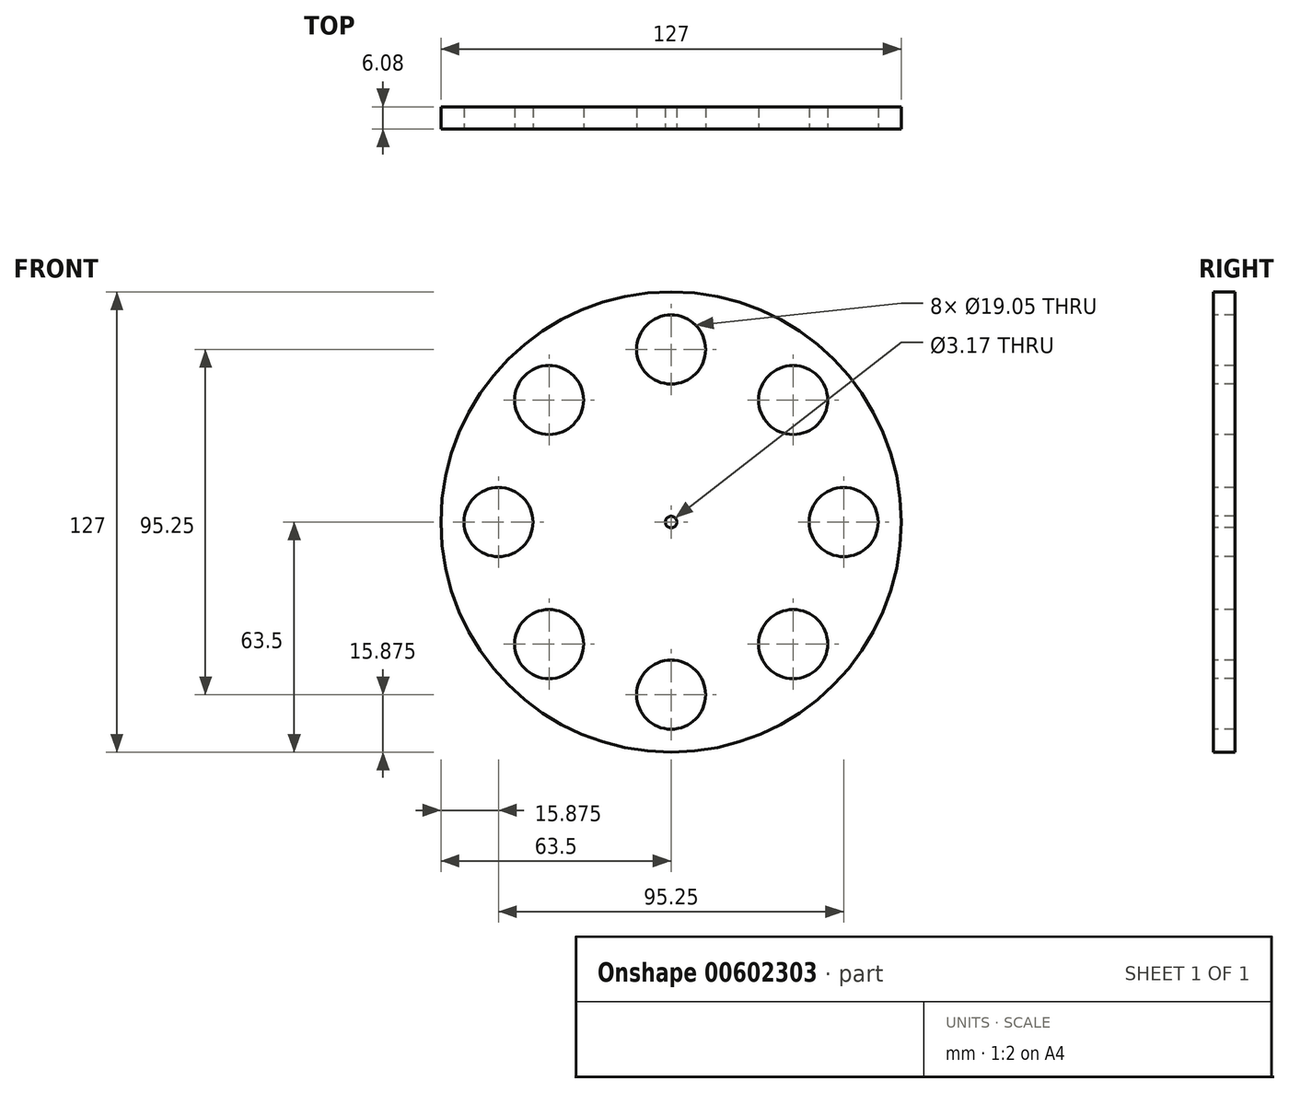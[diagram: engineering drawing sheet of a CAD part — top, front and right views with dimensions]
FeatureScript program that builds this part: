
annotation { "Feature Type Name" : "Feature", "Feature Type Description" : "" }
export const myFeature = defineFeature(function(context is Context, id is Id, definition is map)
    precondition{}
    {
        {
            var Q0;
            Q0=qCreatedBy(makeId("Front.planeOp"),FACE);
            var sketch = newSketch(context, id + "F0", { "sketchPlane" : qUnion([Q0])});
            skCircle(sketch, "E0", {"center": v(0, 0) * mm, "radius": 63.5 * mm});
            skSolve(sketch);
        }
        {
            var Q0;
            Q0=qSketchRegion(id+"F0",true);
            extrude(context, id + "F1", {"entities" : qUnion([Q0]), "depth" : 6.08 * mm});
        }
        {
            var Q0;
            Q0=makeQuery(id+"F1.opExtrude","CAP_FACE",FACE,{"disambiguationData":[OSD([sQuery(id+"F0.wireOp",EDGE,"E0")])],"isStart":false});
            var sketch = newSketch(context, id + "F2", { "sketchPlane" : qUnion([Q0])});
            skCircle(sketch, "E1", {"center": v(0, 0) * mm, "radius": 1.59 * mm});
            skLineSegment(sketch, "E2", {"start": v(-63.5, 0) * mm, "end": v(0, 0) * mm});
            skLineSegment(sketch, "E3", {"start": v(0, 63.5) * mm, "end": v(0, 0) * mm});
            skLineSegment(sketch, "E4", {"start": v(0, 0) * mm, "end": v(0, -63.5) * mm});
            skLineSegment(sketch, "E5", {"start": v(0, -63.5) * mm, "end": v(0, 0) * mm});
            skLineSegment(sketch, "E6", {"start": v(63.5, 0) * mm, "end": v(0, 0) * mm});
            skLineSegment(sketch, "E7", {"start": v(0, 0) * mm, "end": v(-44.9, 44.9) * mm});
            skLineSegment(sketch, "E8", {"start": v(0, 0) * mm, "end": v(44.9, 44.9) * mm});
            skLineSegment(sketch, "E9", {"start": v(0, 0) * mm, "end": v(44.9, -44.9) * mm});
            skLineSegment(sketch, "E10", {"start": v(0, 0) * mm, "end": v(-44.9, -44.9) * mm});
            skLineSegment(sketch, "E11", {"start": v(0, 0) * mm, "end": v(-58.67, -24.3) * mm});
            skLineSegment(sketch, "E12", {"start": v(0, 0) * mm, "end": v(-24.3, -58.67) * mm});
            skLineSegment(sketch, "E13", {"start": v(0, 0) * mm, "end": v(24.3, -58.67) * mm});
            skLineSegment(sketch, "E14", {"start": v(0, 0) * mm, "end": v(58.67, -24.3) * mm});
            skLineSegment(sketch, "E15", {"start": v(0, 0) * mm, "end": v(58.67, 24.3) * mm});
            skLineSegment(sketch, "E16", {"start": v(0, 0) * mm, "end": v(24.3, 58.67) * mm});
            skLineSegment(sketch, "E17", {"start": v(0, 0) * mm, "end": v(-24.3, 58.67) * mm});
            skLineSegment(sketch, "E18", {"start": v(0, 0) * mm, "end": v(-58.67, 24.3) * mm});
            skLineSegment(sketch, "E19", {"start": v(-22.45, 22.45) * mm, "end": v(-44.9, 44.9) * mm});
            skCircle(sketch, "E20", {"center": v(-33.68, 33.68) * mm, "radius": 9.53 * mm});
            skLineSegment(sketch, "E21", {"start": v(0, 31.75) * mm, "end": v(0, 63.5) * mm});
            skLineSegment(sketch, "E22", {"start": v(44.9, 44.9) * mm, "end": v(22.45, 22.45) * mm});
            skLineSegment(sketch, "E23", {"start": v(31.75, 0) * mm, "end": v(63.5, 0) * mm});
            skLineSegment(sketch, "E24", {"start": v(44.9, -44.9) * mm, "end": v(22.45, -22.45) * mm});
            skLineSegment(sketch, "E25", {"start": v(0, -63.5) * mm, "end": v(0, -31.75) * mm});
            skLineSegment(sketch, "E26", {"start": v(-44.9, -44.9) * mm, "end": v(-22.45, -22.45) * mm});
            skLineSegment(sketch, "E27", {"start": v(-63.5, 0) * mm, "end": v(-31.75, 0) * mm});
            skCircle(sketch, "E28", {"center": v(-47.62, 0) * mm, "radius": 9.53 * mm});
            skCircle(sketch, "E29", {"center": v(0, 47.62) * mm, "radius": 9.53 * mm});
            skCircle(sketch, "E30", {"center": v(33.68, 33.68) * mm, "radius": 9.53 * mm});
            skCircle(sketch, "E31", {"center": v(47.62, 0) * mm, "radius": 9.53 * mm});
            skCircle(sketch, "E32", {"center": v(33.68, -33.68) * mm, "radius": 9.53 * mm});
            skCircle(sketch, "E33", {"center": v(0, -47.62) * mm, "radius": 9.53 * mm});
            skCircle(sketch, "E34", {"center": v(-33.68, -33.68) * mm, "radius": 9.53 * mm});
            skSolve(sketch);
        }
        {
            var Q0;
            Q0=qSketchRegion(id+"F2",true);
            extrude(context, id + "F3", {"entities" : qUnion([Q0]), "operationType" : NewBodyOperationType.REMOVE, "oppositeDirection" : true, "depth" : 25.4 * mm});
        }
        {
            var Q0;
            Q0=qSketchRegion(id+"F2",true);
            extrude(context, id + "F4", {"entities" : qUnion([Q0]), "operationType" : NewBodyOperationType.REMOVE, "oppositeDirection" : true, "depth" : 25.4 * mm});
        }
    });
